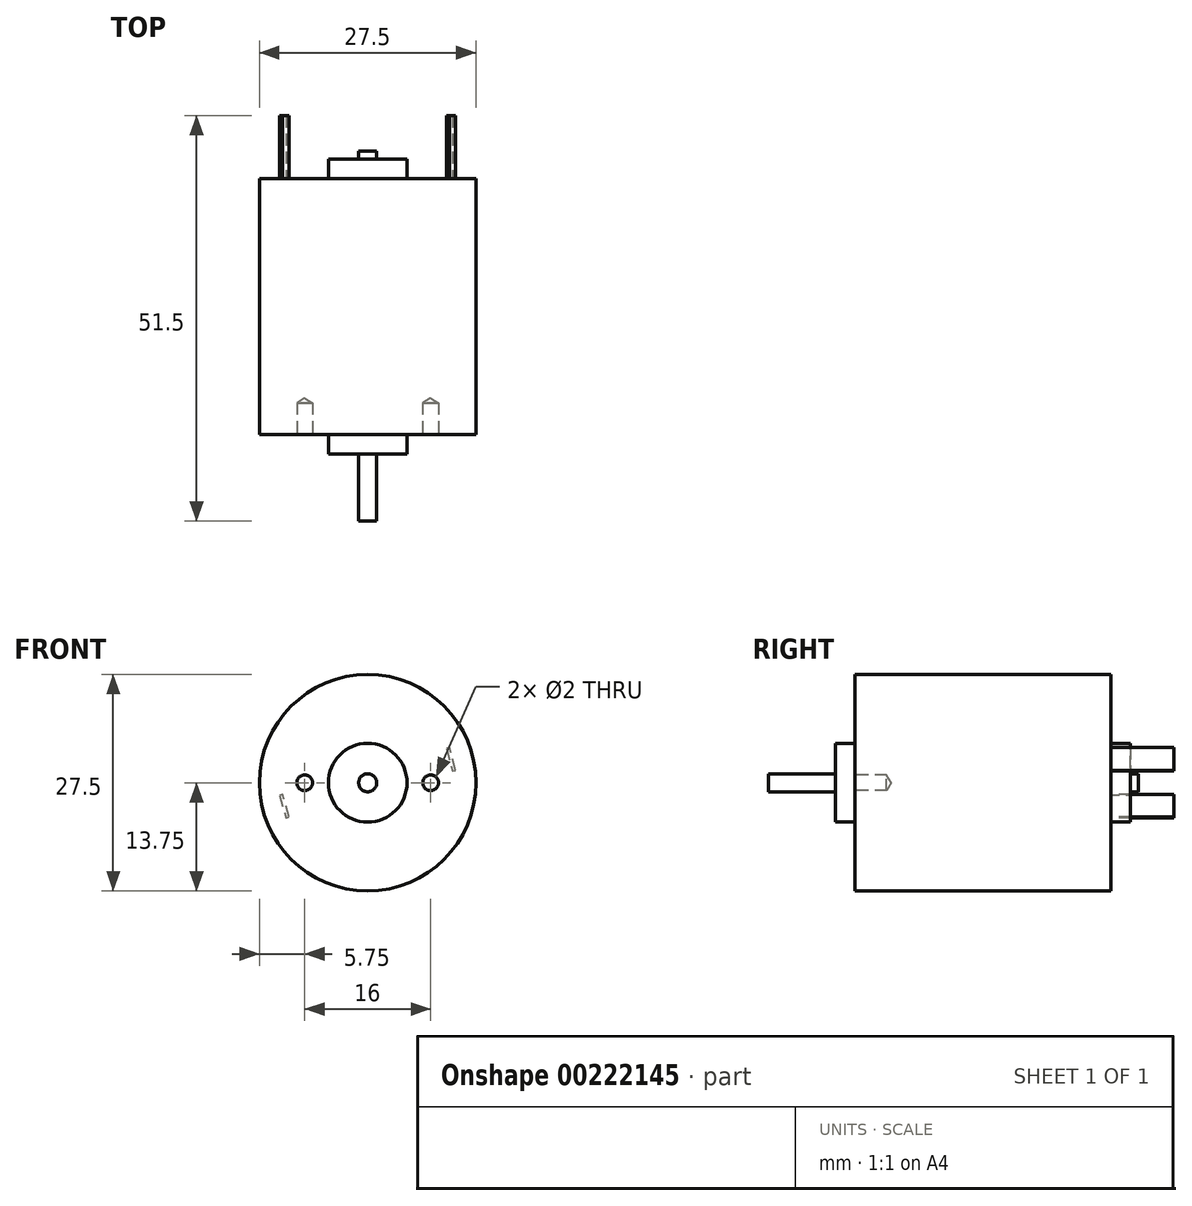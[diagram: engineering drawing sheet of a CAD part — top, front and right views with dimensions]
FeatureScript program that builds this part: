
annotation { "Feature Type Name" : "Feature", "Feature Type Description" : "" }
export const myFeature = defineFeature(function(context is Context, id is Id, definition is map)
    precondition{}
    {
        {
            var Q0;
            Q0=qCreatedBy(makeId("Front.planeOp"),FACE);
            var sketch = newSketch(context, id + "F0", { "sketchPlane" : qUnion([Q0])});
            skCircle(sketch, "E0", {"center": v(0, 0) * mm, "radius": 13.75 * mm});
            skSolve(sketch);
        }
        {
            var Q0;
            Q0 = qSketchRegion(id + "F0", true);
            extrude(context, id + "F1", {"entities" : qUnion([Q0]), "oppositeDirection" : true, "depth" : 32.5 * mm});
        }
        {
            var Q0;
            Q0=makeQuery(id+"F1.opExtrude","CAP_FACE",FACE,{"disambiguationData":[OSD([sQuery(id+"F0.wireOp",EDGE,"E0")])],"isStart":true});
            var sketch = newSketch(context, id + "F2", { "sketchPlane" : qUnion([Q0])});
            skCircle(sketch, "E1", {"center": v(0, 0) * mm, "radius": 5 * mm});
            skSolve(sketch);
        }
        {
            var Q0;
            Q0 = qSketchRegion(id + "F2", true);
            extrude(context, id + "F3", {"entities" : qUnion([Q0]), "operationType" : NewBodyOperationType.ADD, "depth" : 2.5 * mm});
        }
        {
            var Q0;
            Q0=makeQuery(id+"F1.opExtrude","CAP_FACE",FACE,{"disambiguationData":[OSD([sQuery(id+"F0.wireOp",EDGE,"E0")])],"isStart":false});
            var sketch = newSketch(context, id + "F4", { "sketchPlane" : qUnion([Q0])});
            skCircle(sketch, "E2", {"center": v(0, 0) * mm, "radius": 5 * mm});
            skSolve(sketch);
        }
        {
            var Q0;
            Q0 = qSketchRegion(id + "F4", true);
            extrude(context, id + "F5", {"entities" : qUnion([Q0]), "operationType" : NewBodyOperationType.ADD, "depth" : 2.5 * mm});
        }
        {
            var Q0;
            Q0=makeQuery(id+"F1.opExtrude","CAP_FACE",FACE,{"disambiguationData":[OSD([sQuery(id+"F0.wireOp",EDGE,"E0")])],"isStart":true});
            var sketch = newSketch(context, id + "F6", { "sketchPlane" : qUnion([Q0])});
            skCircle(sketch, "E3", {"center": v(0, 0) * mm, "radius": 8 * mm, "construction": true});
            skCircle(sketch, "E4", {"center": v(8, 0) * mm, "radius": 1 * mm});
            skCircle(sketch, "E5.1.0", {"center": v(-8, 0) * mm, "radius": 1 * mm});
            skLineSegment(sketch, "E5.anchor1", {"start": v(0, 0) * mm, "end": v(8, 0) * mm, "construction": true});
            skLineSegment(sketch, "E5.anchor2", {"start": v(0, 0) * mm, "end": v(-8, 0) * mm, "construction": true});
            skSolve(sketch);
        }
        {
            var Q0;
            Q0=sQuery(id+"F6.wireOp",VERTEX,"E5.1.0.center");
            var Q1;
            Q1=sQuery(id+"F6.wireOp",VERTEX,"E4.center");
            var Q2;
            Q2=makeQuery(id+"F1.opExtrude","SWEPT_BODY",BODY,{"disambiguationData":[OSD([sQuery(id+"F0.wireOp",EDGE,"E0")])]});
            hole(context, id + "F7", {"style" : HoleStyle.SIMPLE, "endStyle" : HoleEndStyle.BLIND, "holeDiameter" : 2 * mm, "holeDepth" : 4 * mm, "locations" : qUnion([Q0, Q1]), "scope" : qUnion([Q2])});
        }
        {
            var Q0;
            Q0=makeQuery(id+"F1.opExtrude","CAP_FACE",FACE,{"disambiguationData":[OSD([sQuery(id+"F0.wireOp",EDGE,"E0")])],"isStart":false});
            var sketch = newSketch(context, id + "F8", { "sketchPlane" : qUnion([Q0])});
            skCircle(sketch, "E6", {"center": v(0, 0) * mm, "radius": 11 * mm, "construction": true});
            skCircle(sketch, "E7", {"center": v(11, 0) * mm, "radius": 3 * mm, "construction": true});
            skLineSegment(sketch, "E8", {"start": v(11, -1.53) * mm, "end": v(11.19, -1.58) * mm});
            skLineSegment(sketch, "E9", {"start": v(11.19, -1.58) * mm, "end": v(10.38, -4.47) * mm});
            skLineSegment(sketch, "E10", {"start": v(10.38, -4.47) * mm, "end": v(10, -4.36) * mm});
            skLineSegment(sketch, "E11", {"start": v(10, -4.36) * mm, "end": v(10.8, -1.47) * mm});
            skLineSegment(sketch, "E12", {"start": v(10.8, -1.47) * mm, "end": v(11.19, -1.58) * mm});
            skLineSegment(sketch, "E13.1.0", {"start": v(-10, 4.36) * mm, "end": v(-10.8, 1.47) * mm});
            skLineSegment(sketch, "E13.1.1", {"start": v(-11.19, 1.58) * mm, "end": v(-10.38, 4.47) * mm});
            skLineSegment(sketch, "E13.1.2", {"start": v(-10.38, 4.47) * mm, "end": v(-10, 4.36) * mm});
            skLineSegment(sketch, "E13.1.3", {"start": v(-10.8, 1.47) * mm, "end": v(-11.19, 1.58) * mm});
            skLineSegment(sketch, "E13.1.4", {"start": v(-11, 1.53) * mm, "end": v(-11.19, 1.58) * mm});
            skSolve(sketch);
        }
        {
            var Q0;
            Q0 = qSketchRegion(id + "F8", true);
            extrude(context, id + "F9", {"entities" : qUnion([Q0]), "operationType" : NewBodyOperationType.ADD, "depth" : 8 * mm});
        }
        {
            var Q0;
            Q0=makeQuery(id+"F3.opExtrude","CAP_FACE",FACE,{"disambiguationData":[OSD([sQuery(id+"F2.wireOp",EDGE,"E1")])],"isStart":false});
            var sketch = newSketch(context, id + "F10", { "sketchPlane" : qUnion([Q0])});
            skCircle(sketch, "E14", {"center": v(0, 0) * mm, "radius": 1.15 * mm});
            skSolve(sketch);
        }
        {
            var Q0;
            Q0 = qSketchRegion(id + "F10", true);
            extrude(context, id + "F11", {"entities" : qUnion([Q0]), "operationType" : NewBodyOperationType.REMOVE, "endBound" : BoundingType.THROUGH_ALL, "oppositeDirection" : true, "depth" : 25 * mm});
        }
        {
            var Q0;
            Q0=makeQuery(id+"F3.opExtrude","CAP_FACE",FACE,{"disambiguationData":[OSD([sQuery(id+"F2.wireOp",EDGE,"E1")])],"isStart":false});
            var sketch = newSketch(context, id + "F12", { "sketchPlane" : qUnion([Q0])});
            skCircle(sketch, "E15", {"center": v(0, 0) * mm, "radius": 1.15 * mm});
            skSolve(sketch);
        }
        {
            var Q0;
            Q0 = qSketchRegion(id + "F12", true);
            extrude(context, id + "F13", {"entities" : qUnion([Q0]), "oppositeDirection" : true, "depth" : 38.5 * mm});
        }
        {
            var Q0;
            Q0=makeQuery(id+"F13.opExtrude","CAP_FACE",FACE,{"disambiguationData":[OSD([sQuery(id+"F12.wireOp",EDGE,"E15")])],"isStart":true});
            var sketch = newSketch(context, id + "F14", { "sketchPlane" : qUnion([Q0])});
            skCircle(sketch, "E16", {"center": v(0, 0) * mm, "radius": 1.15 * mm});
            skSolve(sketch);
        }
        {
            var Q0;
            Q0 = qSketchRegion(id + "F14", true);
            extrude(context, id + "F15", {"entities" : qUnion([Q0]), "operationType" : NewBodyOperationType.ADD, "depth" : 8.5 * mm});
        }
    });
